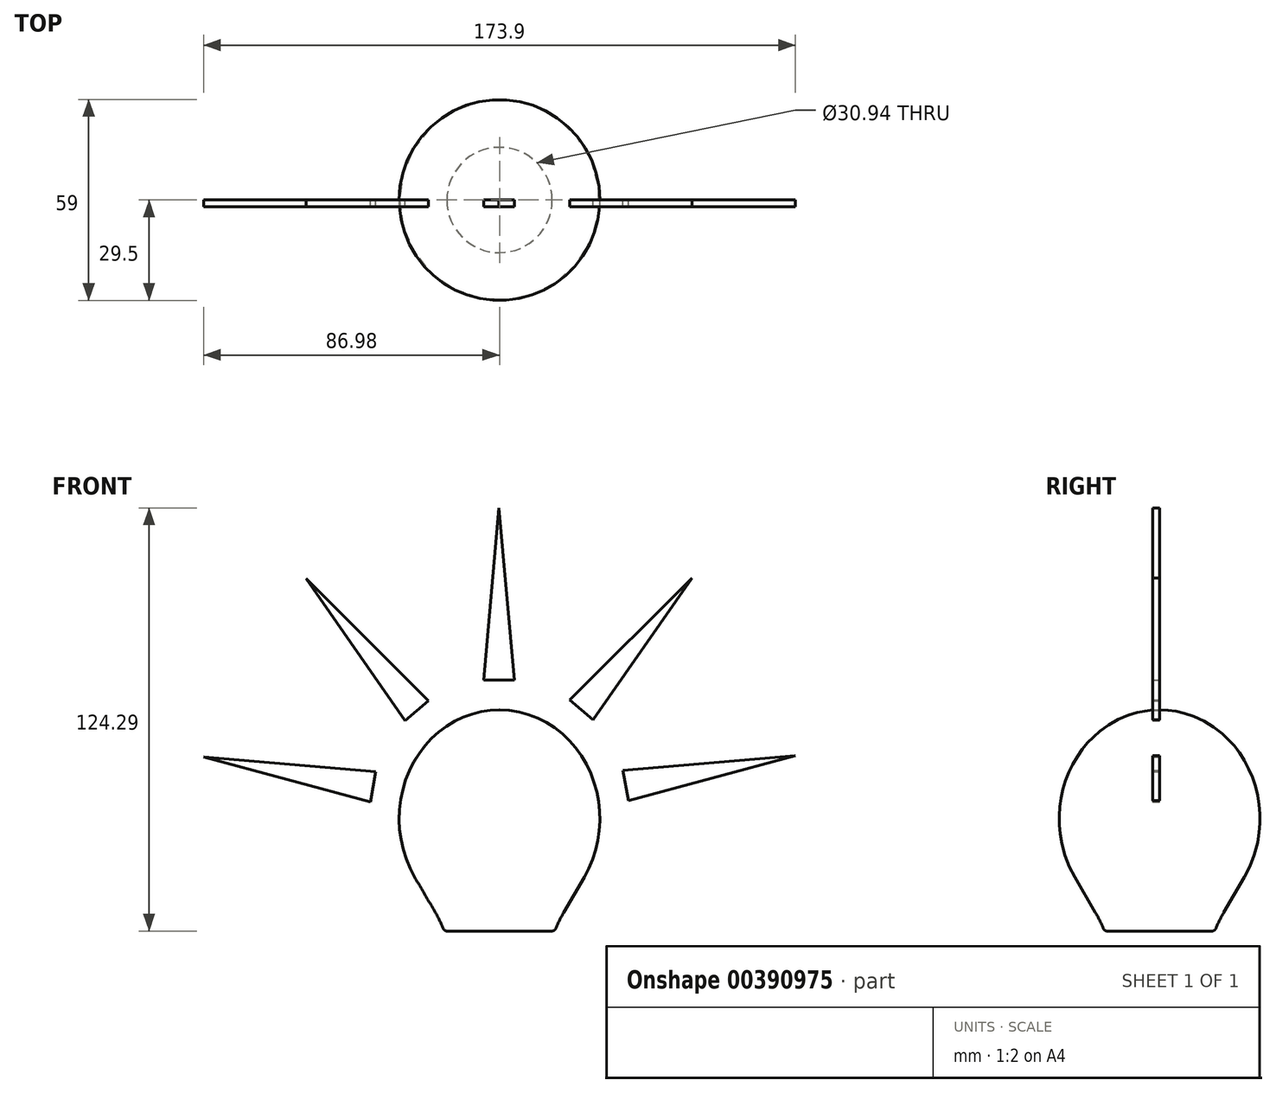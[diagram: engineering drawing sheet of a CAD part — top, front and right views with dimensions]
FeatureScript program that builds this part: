
annotation { "Feature Type Name" : "Feature", "Feature Type Description" : "" }
export const myFeature = defineFeature(function(context is Context, id is Id, definition is map)
    precondition{}
    {
        {
            var Q0;
            Q0=qCreatedBy(makeId("Front.planeOp"),FACE);
            var sketch = newSketch(context, id + "F0", { "sketchPlane" : qUnion([Q0])});
            skLineSegment(sketch, "E0", {"start": v(0, 0) * mm, "end": v(0, 65) * mm});
            skPoint(sketch, "E1", {"position": v(0, 32.5) * mm});
            skPoint(sketch, "E2.orphan", {"position": v(-21.04, 26.04) * mm});
            skPoint(sketch, "E3.orphan", {"position": v(-21.04, 0) * mm});
            skLineSegment(sketch, "E4", {"start": v(-15.47, 0) * mm, "end": v(0, 0) * mm});
            skPoint(sketch, "E5.second.point", {"position": v(0, 8.98) * mm});
            skPoint(sketch, "E5.third.point", {"position": v(-24.57, 58.48) * mm});
            skEllipticalArc(sketch, "E6", {});
            skPoint(sketch, "E7.orphan", {"position": v(-21.04, 14.06) * mm});
            skLineSegment(sketch, "E8", {"start": v(-24.92, 15.83) * mm, "end": v(-18.87, 5.47) * mm});
            skPoint(sketch, "E9.visualSharp", {"position": v(-20.34, 7.97) * mm});
            skArc(sketch, "E9.filletArc", {"start": v(-16.5, 0.69) * mm, "mid": v(-17.6, 3.12) * mm, "end": v(-18.87, 5.47) * mm});
            skPoint(sketch, "E10.visualSharp", {"position": v(-16, 0) * mm});
            skArc(sketch, "E10.filletArc", {"start": v(-16.5, 0.69) * mm, "mid": v(-16.09, 0.19) * mm, "end": v(-15.47, 0) * mm});
            const initialGuessF0  = {"E6": [0, 0.03297137370965459, 0, 1, 0.03202862629034541, 0.0295, 0, 2.1355146130499993]};
            skSetInitialGuess(sketch, initialGuessF0);
            skSolve(sketch);
        }
        {
            var Q0;
            Q0=qSketchRegion(id+"F0",true);
            var Q1;
            Q1=sQuery(id+"F0.wireOp",EDGE,"E0");
            revolve(context, id + "F1", {"entities" : qUnion([Q0]), "axis" : qUnion([Q1]), "revolveType" : RevolveType.FULL});
        }
        {
            var Q0;
            Q0=makeQuery(id+"F1.opRevolve","SWEPT_FACE",FACE,{"disambiguationData":[OSD([sQuery(id+"F0.wireOp",EDGE,"E4")])]});
            shell(context, id + "F2", {"entities" : qUnion([Q0]), "thickness" : 0.1 * mm});
        }
        {
            var Q0;
            Q0=qCreatedBy(makeId("Front.planeOp"),FACE);
            var sketch = newSketch(context, id + "F3", { "sketchPlane" : qUnion([Q0])});
            skLineSegment(sketch, "E11", {"start": v(-0.17, -46.52) * mm, "end": v(-0.17, 124.29) * mm, "construction": true});
            skLineSegment(sketch, "E12", {"start": v(-0.17, 124.29) * mm, "end": v(-4.69, 73.7) * mm});
            skLineSegment(sketch, "E13.MirrorCS", {"start": v(-0.17, 124.29) * mm, "end": v(4.34, 73.7) * mm});
            skLineSegment(sketch, "E14", {"start": v(-4.69, 73.7) * mm, "end": v(4.34, 73.7) * mm});
            skSolve(sketch);
        }
        {
            var Q0;
            Q0=qSketchRegion(id+"F3",true);
            extrude(context, id + "F4", {"entities" : qUnion([Q0]), "depth" : 2 * mm});
        }
        {
            var Q0;
            Q0=qCreatedBy(makeId("Front.planeOp"),FACE);
            var sketch = newSketch(context, id + "F5", { "sketchPlane" : qUnion([Q0])});
            skCircle(sketch, "E15", {"center": v(0, 36) * mm, "radius": 38.35 * mm, "construction": true});
            skSolve(sketch);
        }
        {
            var Q0;
            Q0=makeQuery(id+"F4.opExtrude","SWEPT_BODY",BODY,{"disambiguationData":[OSD([sQuery(id+"F3.wireOp",EDGE,"E12"),sQuery(id+"F3.wireOp",EDGE,"E13.MirrorCS"),sQuery(id+"F3.wireOp",EDGE,"E14")])]});
            var Q1;
            Q1=sQuery(id+"F5.wireOp",EDGE,"E15");
            circularPattern(context, id + "F6", {"entities" : qUnion([Q0]), "axis" : qUnion([Q1]), "angle" : 40 * degree, "instanceCount" : 3, "oppositeDirection" : true});
        }
        {
            var Q0;
            Q0=makeQuery(id+"F4.opExtrude","SWEPT_BODY",BODY,{"disambiguationData":[OSD([sQuery(id+"F3.wireOp",EDGE,"E12"),sQuery(id+"F3.wireOp",EDGE,"E13.MirrorCS"),sQuery(id+"F3.wireOp",EDGE,"E14")])]});
            var Q1;
            Q1=sQuery(id+"F5.wireOp",EDGE,"E15");
            circularPattern(context, id + "F7", {"entities" : qUnion([Q0]), "axis" : qUnion([Q1]), "angle" : 40 * degree, "instanceCount" : 3});
        }
    });
